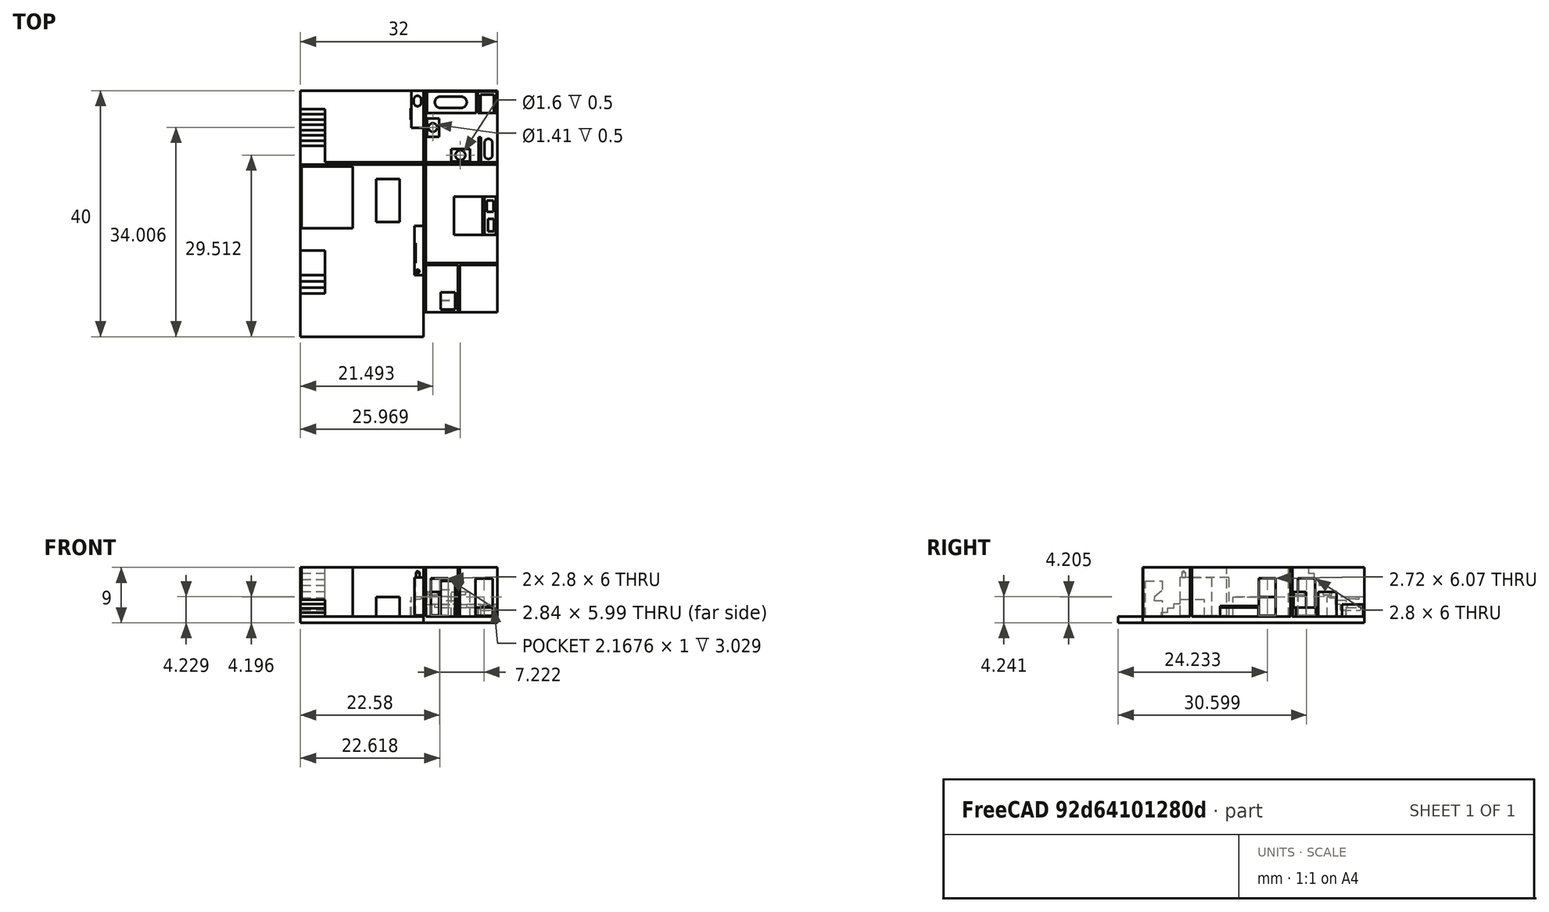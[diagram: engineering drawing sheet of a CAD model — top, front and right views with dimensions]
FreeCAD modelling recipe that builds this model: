
FCSTD DOCUMENT  (FreeCAD 0.19R)
Label: Addition1D_dualCloset
License: All rights reserved
LicenseURL: http://en.wikipedia.org/wiki/All_rights_reserved
objects: Sketcher::SketchObject×28, PartDesign::Pad×17, PartDesign::Pocket×10, PartDesign::Chamfer×1, PartDesign::Body×1, Mesh::Feature×1
note: 85 computed .brp shape members not serialized (recipe doc carries the construction recipe); baked Part::Feature solids carry a one-line shape summary decoded from their .brp

FEATURE [Sketcher::SketchObject] Sketch
  FullyConstrained = true
  MapMode = 5
  Support = -> [XY_Plane]
  sketch-geometry (8):
    g0: LineSegment StartX=0 StartY=-28 StartZ=0 EndX=-20 EndY=-28 EndZ=0
    g1: LineSegment StartX=-20 StartY=-28 StartZ=0 EndX=-20 EndY=0 EndZ=0
    g2: LineSegment StartX=-20 StartY=0 StartZ=0 EndX=-16 EndY=0 EndZ=0
    g3: LineSegment StartX=-16 StartY=0 StartZ=0 EndX=-16 EndY=12 EndZ=0
    g4: LineSegment StartX=-16 StartY=12 StartZ=0 EndX=12 EndY=12 EndZ=0
    g5: LineSegment StartX=12 StartY=12 StartZ=0 EndX=12 EndY=-24 EndZ=0
    g6: LineSegment StartX=12 StartY=-24 StartZ=0 EndX=0 EndY=-24 EndZ=0
    g7: LineSegment StartX=0 StartY=-24 StartZ=0 EndX=0 EndY=-28 EndZ=0
  constraints (24):
    c: Coincident(g0,g1)
    c: Horizontal(g0)
    c: Vertical(g1)
    c: DistanceX(g1) = -20
    c: DistanceY(g0) = -28
    c: Coincident(g1,g2)
    c: PointOnObject(g2,g-1)
    c: Horizontal(g2)
    c: Coincident(g2,g3)
    c: Vertical(g3)
    c: Coincident(g3,g4)
    c: Horizontal(g4)
    c: Coincident(g4,g5)
    c: Vertical(g5)
    c: Coincident(g5,g6)
    c: PointOnObject(g6,g-2)
    c: Coincident(g6,g7)
    c: Coincident(g7,g0)
    c: Vertical(g7)
    c: Horizontal(g6)
    c: Distance(g6) = 12
    c: Distance(g3) = 12
    c: DistanceY(g6) = -24
    c: DistanceX(g2) = -16
FEATURE [PartDesign::Pad] Pad  label="foundation"
  Direction = (1,1,1)
  Length = 1
  Length2 = 100
  Profile = -> Sketch
  Type = 0
FEATURE [Sketcher::SketchObject] Sketch004
  FullyConstrained = true
  MapMode = 5
  Placement = pos=(-16,0,0) rot=(0.57735,-0.57735,-0.57735;2.0944rad)
  Support = -> [Pad]
  sketch-geometry (20):
    g0: LineSegment StartX=-12 StartY=0 StartZ=0 EndX=-12 EndY=1 EndZ=0
    g1: LineSegment StartX=-12 StartY=1 StartZ=0 EndX=-9 EndY=1 EndZ=0
    g2: LineSegment StartX=-9 StartY=1 StartZ=0 EndX=-9 EndY=2 EndZ=0
    g3: LineSegment StartX=-9 StartY=2 StartZ=0 EndX=-8.14286 EndY=2 EndZ=0
    g4: LineSegment StartX=-8.14286 StartY=2 StartZ=0 EndX=-8.14286 EndY=3 EndZ=0
    g5: LineSegment StartX=-8.14286 StartY=3 StartZ=0 EndX=-7.28571 EndY=3 EndZ=0
    g6: LineSegment StartX=-7.28571 StartY=3 StartZ=0 EndX=-7.28571 EndY=4 EndZ=0
    g7: LineSegment StartX=-7.28571 StartY=4 StartZ=0 EndX=-6.42857 EndY=4 EndZ=0
    g8: LineSegment StartX=-6.42857 StartY=4 StartZ=0 EndX=-6.42857 EndY=5 EndZ=0
    g9: LineSegment StartX=-6.42857 StartY=5 StartZ=0 EndX=-5.57143 EndY=5 EndZ=0
    g10: LineSegment StartX=-5.57143 StartY=5 StartZ=0 EndX=-5.57143 EndY=6 EndZ=0
    g11: LineSegment StartX=-5.57143 StartY=6 StartZ=0 EndX=-4.71429 EndY=6 EndZ=0
    g12: LineSegment StartX=-4.71429 StartY=6 StartZ=0 EndX=-4.71429 EndY=7 EndZ=0
    g13: LineSegment StartX=-4.71429 StartY=7 StartZ=0 EndX=-3.85714 EndY=7 EndZ=0
    g14: LineSegment StartX=-3.85714 StartY=7 StartZ=0 EndX=-3.85714 EndY=8 EndZ=0
    g15: LineSegment StartX=-3.85714 StartY=8 StartZ=0 EndX=-3 EndY=8 EndZ=0
    g16: LineSegment StartX=-3 StartY=8 StartZ=0 EndX=-3 EndY=9 EndZ=0
    g17: LineSegment StartX=-3 StartY=9 StartZ=0 EndX=0 EndY=9 EndZ=0
    g18: LineSegment StartX=0 StartY=9 StartZ=0 EndX=0 EndY=0 EndZ=0
    g19: LineSegment StartX=0 StartY=0 StartZ=0 EndX=-12 EndY=0 EndZ=0
  constraints (59):
    c: PointOnObject(g0,g-1)
    c: Coincident(g0,g1)
    c: Coincident(g1,g2)
    c: Coincident(g2,g3)
    c: Coincident(g3,g4)
    c: Vertical(g4)
    c: Coincident(g4,g5)
    c: Horizontal(g5)
    c: Coincident(g5,g6)
    c: Coincident(g6,g7)
    c: Coincident(g7,g8)
    c: Coincident(g8,g9)
    c: Coincident(g9,g10)
    c: Coincident(g10,g11)
    c: Horizontal(g11)
    c: Coincident(g11,g12)
    c: Coincident(g12,g13)
    c: Coincident(g13,g14)
    c: Coincident(g14,g15)
    c: Coincident(g15,g16)
    c: Coincident(g16,g17)
    c: PointOnObject(g17,g-2)
    c: Coincident(g17,g18)
    c: Coincident(g18,g-1)
    c: Coincident(g18,g19)
    c: Coincident(g19,g0)
    c: DistanceY(g17) = 9
    c: Horizontal(g3)
    c: Horizontal(g7)
    c: Horizontal(g9)
    c: Horizontal(g13)
    c: Horizontal(g15)
    c: Vertical(g6)
    c: Vertical(g8)
    c: Vertical(g12)
    c: Vertical(g10)
    c: Vertical(g14)
    c: Vertical(g16)
    c: Vertical(g2)
    c: Equal(g2,g4)
    c: Equal(g4,g6)
    c: Equal(g6,g8)
    c: Equal(g8,g10)
    c: Equal(g10,g12)
    c: Equal(g12,g14)
    c: Equal(g14,g16)
    c: Distance(g17) = 3
    c: Equal(g3,g5)
    c: Equal(g5,g7)
    c: Equal(g7,g9)
    c: Equal(g9,g11)
    c: Equal(g11,g13)
    c: Equal(g13,g15)
    c: Horizontal(g1)
    c: Horizontal(g17)
    c: Distance(g1) = 3
    c: Vertical(g0)
    c: Distance(g0) = 1
    c: DistanceX(g0) = -12
FEATURE [Sketcher::SketchObject] Sketch007
  FullyConstrained = true
  MapMode = 5
  Placement = pos=(0,0,1) rot=(0,0,1;0rad)
  sketch-geometry (16):
    g0: LineSegment StartX=0.33 StartY=12 StartZ=0 EndX=0.33 EndY=-24 EndZ=0
    g1: LineSegment StartX=0.33 StartY=-24 StartZ=0 EndX=0 EndY=-24 EndZ=0
    g2: LineSegment StartX=0 StartY=-24 StartZ=0 EndX=0 EndY=12 EndZ=0
    g3: LineSegment StartX=0 StartY=12 StartZ=0 EndX=0.33 EndY=12 EndZ=0
    g4: LineSegment StartX=0.33 StartY=0.33 StartZ=0 EndX=12 EndY=0.33 EndZ=0
    g5: LineSegment StartX=12 StartY=0.33 StartZ=0 EndX=12 EndY=0 EndZ=0
    g6: LineSegment StartX=12 StartY=0 StartZ=0 EndX=0.33 EndY=0 EndZ=0
    g7: LineSegment StartX=0.33 StartY=0 StartZ=0 EndX=0.33 EndY=0.33 EndZ=0
    g8: LineSegment StartX=-16 StartY=0.33 StartZ=0 EndX=0 EndY=0.33 EndZ=0
    g9: LineSegment StartX=0 StartY=0.33 StartZ=0 EndX=0 EndY=0 EndZ=0
    g10: LineSegment StartX=0 StartY=0 StartZ=0 EndX=-16 EndY=0 EndZ=0
    g11: LineSegment StartX=-16 StartY=0 StartZ=0 EndX=-16 EndY=0.33 EndZ=0
    g12: LineSegment StartX=0.33 StartY=-16.33 StartZ=0 EndX=12 EndY=-16.33 EndZ=0
    g13: LineSegment StartX=12 StartY=-16.33 StartZ=0 EndX=12 EndY=-16 EndZ=0
    g14: LineSegment StartX=12 StartY=-16 StartZ=0 EndX=0.33 EndY=-16 EndZ=0
    g15: LineSegment StartX=0.33 StartY=-16 StartZ=0 EndX=0.33 EndY=-16.33 EndZ=0
  constraints (47):
    c: Coincident(g0,g1)
    c: Coincident(g1,g2)
    c: Horizontal(g1)
    c: Vertical(g0)
    c: Vertical(g2)
    c: DistanceY(g2) = 12
    c: PointOnObject(g-1,g2)
    c: Coincident(g3,g2)
    c: Coincident(g3,g0)
    c: Horizontal(g3)
    c: Distance(g3) = 0.33
    c: DistanceY(g0) = -24
    c: Coincident(g4,g5)
    c: Coincident(g5,g6)
    c: Coincident(g6,g7)
    c: Coincident(g7,g4)
    c: Horizontal(g4)
    c: Horizontal(g6)
    c: Vertical(g5)
    c: Vertical(g7)
    c: PointOnObject(g5,g-1)
    c: Coincident(g8,g9)
    c: Coincident(g9,g10)
    c: Coincident(g10,g11)
    c: Coincident(g11,g8)
    c: Horizontal(g8)
    c: Horizontal(g10)
    c: Vertical(g9)
    c: Vertical(g11)
    c: Coincident(g9,g-1)
    c: Coincident(g12,g13)
    c: Coincident(g13,g14)
    c: Coincident(g14,g15)
    c: Coincident(g15,g12)
    c: Horizontal(g12)
    c: Horizontal(g14)
    c: Vertical(g13)
    c: Vertical(g15)
    c: PointOnObject(g12,g0)
    c: Distance(g11) = 0.33
    c: Distance(g5) = 0.33
    c: DistanceX(g4) = 12
    c: DistanceX(g8) = -16
    c: PointOnObject(g4,g0)
    c: Distance(g13) = 0.33
    c: Distance(g0,g14) = 8
    c: DistanceX(g13) = 12
FEATURE [PartDesign::Pad] Pad004  label="wall"
  BaseFeature = -> Pad
  Direction = (1,1,1)
  Length = 8
  Length2 = 100
  Profile = -> Sketch007
  Type = 0
FEATURE [PartDesign::Pad] Pad005  label="stairs001"
  BaseFeature = -> Pad004
  Direction = (1,1,1)
  Length = 4
  Length2 = 100
  Profile = -> Sketch004
  Type = 0
FEATURE [Sketcher::SketchObject] Sketch008
  FullyConstrained = false
  MapMode = 5
  Placement = pos=(0,-16.33,0) rot=(1,0,0;1.5708rad)
  Support = -> [Pad005]
  sketch-geometry (8):
    g0: LineSegment StartX=1.18012 StartY=7.22945 StartZ=0 EndX=3.98012 EndY=7.22945 EndZ=0
    g1: LineSegment StartX=3.98012 StartY=7.22945 StartZ=0 EndX=3.98012 EndY=1.22945 EndZ=0
    g2: LineSegment StartX=3.98012 StartY=1.22945 StartZ=0 EndX=1.18012 EndY=1.22945 EndZ=0
    g3: LineSegment StartX=1.18012 StartY=1.22945 StartZ=0 EndX=1.18012 EndY=7.22945 EndZ=0
    g4: LineSegment StartX=8.40186 StartY=7.15703 StartZ=0 EndX=11.2019 EndY=7.15703 EndZ=0
    g5: LineSegment StartX=11.2019 StartY=7.15703 StartZ=0 EndX=11.2019 EndY=1.15703 EndZ=0
    g6: LineSegment StartX=11.2019 StartY=1.15703 StartZ=0 EndX=8.40186 EndY=1.15703 EndZ=0
    g7: LineSegment StartX=8.40186 StartY=1.15703 StartZ=0 EndX=8.40186 EndY=7.15703 EndZ=0
  constraints (20):
    c: Coincident(g0,g1)
    c: Coincident(g1,g2)
    c: Coincident(g2,g3)
    c: Coincident(g3,g0)
    c: Horizontal(g0)
    c: Horizontal(g2)
    c: Vertical(g1)
    c: Vertical(g3)
    c: Coincident(g4,g5)
    c: Coincident(g5,g6)
    c: Coincident(g6,g7)
    c: Coincident(g7,g4)
    c: Horizontal(g4)
    c: Horizontal(g6)
    c: Vertical(g5)
    c: Vertical(g7)
    c: Distance(g4) = 2.8
    c: Distance(g0) = 2.8
    c: Distance(g1) = 6
    c: Distance(g7) = 6
FEATURE [PartDesign::Pocket] Pocket
  BaseFeature = -> Pad005
  Length = 5
  Length2 = 100
  Profile = -> Sketch008
  Type = 0
FEATURE [Sketcher::SketchObject] Sketch009
  FullyConstrained = false
  MapMode = 5
  Placement = pos=(0,0,0) rot=(1,0,0;1.5708rad)
  Support = -> [Pocket]
  sketch-geometry (4):
    g0: LineSegment StartX=1.19795 StartY=7.19291 StartZ=0 EndX=4.03725 EndY=7.19291 EndZ=0
    g1: LineSegment StartX=4.03725 StartY=7.19291 StartZ=0 EndX=4.03725 EndY=1.19882 EndZ=0
    g2: LineSegment StartX=4.03725 StartY=1.19882 StartZ=0 EndX=1.19795 EndY=1.19882 EndZ=0
    g3: LineSegment StartX=1.19795 StartY=1.19882 StartZ=0 EndX=1.19795 EndY=7.19291 EndZ=0
  constraints (8):
    c: Coincident(g0,g1)
    c: Coincident(g1,g2)
    c: Coincident(g2,g3)
    c: Coincident(g3,g0)
    c: Horizontal(g0)
    c: Horizontal(g2)
    c: Vertical(g1)
    c: Vertical(g3)
FEATURE [PartDesign::Pocket] Pocket001
  BaseFeature = -> Pocket
  Length = 5
  Length2 = 100
  Profile = -> Sketch009
  Type = 0
FEATURE [Sketcher::SketchObject] Sketch010
  FullyConstrained = false
  MapMode = 5
  Placement = pos=(0.33,0,0) rot=(0.57735,0.57735,0.57735;2.0944rad)
  Support = -> [Pocket001]
  sketch-geometry (4):
    g0: LineSegment StartX=1.19868 StartY=7.24093 StartZ=0 EndX=3.99868 EndY=7.24093 EndZ=0
    g1: LineSegment StartX=3.99868 StartY=7.24093 StartZ=0 EndX=3.99868 EndY=1.24093 EndZ=0
    g2: LineSegment StartX=3.99868 StartY=1.24093 StartZ=0 EndX=1.19868 EndY=1.24093 EndZ=0
    g3: LineSegment StartX=1.19868 StartY=1.24093 StartZ=0 EndX=1.19868 EndY=7.24093 EndZ=0
  constraints (10):
    c: Coincident(g0,g1)
    c: Coincident(g1,g2)
    c: Coincident(g2,g3)
    c: Coincident(g3,g0)
    c: Horizontal(g0)
    c: Horizontal(g2)
    c: Vertical(g1)
    c: Vertical(g3)
    c: Distance(g0) = 2.8
    c: Distance(g1) = 6
FEATURE [PartDesign::Pocket] Pocket002
  BaseFeature = -> Pocket001
  Length = 5
  Length2 = 100
  Profile = -> Sketch010
  Type = 0
FEATURE [Sketcher::SketchObject] Sketch011
  FullyConstrained = false
  MapMode = 5
  Placement = pos=(0,0,1) rot=(0,0,1;0rad)
  Support = -> [Pocket002]
  sketch-geometry (8):
    g0: LineSegment StartX=0.512815 StartY=11.8677 StartZ=0 EndX=8.51282 EndY=11.8677 EndZ=0
    g1: LineSegment StartX=8.51282 StartY=11.8677 StartZ=0 EndX=8.51282 EndY=8.36765 EndZ=0
    g2: LineSegment StartX=8.51282 StartY=8.36765 StartZ=0 EndX=0.512815 EndY=8.36765 EndZ=0
    g3: LineSegment StartX=0.512815 StartY=8.36765 StartZ=0 EndX=0.512815 EndY=11.8677 EndZ=0
    g4: LineSegment StartX=8.80064 StartY=11.8358 StartZ=0 EndX=11.8627 EndY=11.8358 EndZ=0
    g5: LineSegment StartX=11.8627 StartY=11.8358 StartZ=0 EndX=11.8627 EndY=8.34693 EndZ=0
    g6: LineSegment StartX=11.8627 StartY=8.34693 StartZ=0 EndX=8.80064 EndY=8.34693 EndZ=0
    g7: LineSegment StartX=8.80064 StartY=8.34693 StartZ=0 EndX=8.80064 EndY=11.8358 EndZ=0
  constraints (18):
    c: Coincident(g0,g1)
    c: Coincident(g1,g2)
    c: Coincident(g2,g3)
    c: Coincident(g3,g0)
    c: Horizontal(g0)
    c: Horizontal(g2)
    c: Vertical(g1)
    c: Vertical(g3)
    c: Coincident(g4,g5)
    c: Coincident(g5,g6)
    c: Coincident(g6,g7)
    c: Coincident(g7,g4)
    c: Horizontal(g4)
    c: Horizontal(g6)
    c: Vertical(g5)
    c: Vertical(g7)
    c: Distance(g0) = 8
    c: Distance(g1) = 3.5
FEATURE [PartDesign::Pad] Pad006
  BaseFeature = -> Pocket002
  Direction = (1,1,1)
  Length = 2
  Length2 = 100
  Profile = -> Sketch011
  Type = 0
FEATURE [Sketcher::SketchObject] Sketch012
  FullyConstrained = false
  MapMode = 5
  Placement = pos=(0,0,1) rot=(0,0,1;0rad)
  Support = -> [Pad006]
  sketch-geometry (8):
    g0: LineSegment StartX=4.5 StartY=2.51571 StartZ=0 EndX=7.5 EndY=2.51571 EndZ=0
    g1: LineSegment StartX=7.5 StartY=2.51571 StartZ=0 EndX=7.5 EndY=0.515713 EndZ=0
    g2: LineSegment StartX=7.5 StartY=0.515713 StartZ=0 EndX=4.5 EndY=0.515713 EndZ=0
    g3: LineSegment StartX=4.5 StartY=0.515713 StartZ=0 EndX=4.5 EndY=2.51571 EndZ=0
    g4: LineSegment StartX=0.518943 StartY=7.5 StartZ=0 EndX=2.51894 EndY=7.5 EndZ=0
    g5: LineSegment StartX=2.51894 StartY=7.5 StartZ=0 EndX=2.51894 EndY=4.5 EndZ=0
    g6: LineSegment StartX=2.51894 StartY=4.5 StartZ=0 EndX=0.518943 EndY=4.5 EndZ=0
    g7: LineSegment StartX=0.518943 StartY=4.5 StartZ=0 EndX=0.518943 EndY=7.5 EndZ=0
  constraints (22):
    c: Coincident(g0,g1)
    c: Coincident(g1,g2)
    c: Coincident(g2,g3)
    c: Coincident(g3,g0)
    c: Horizontal(g0)
    c: Horizontal(g2)
    c: Vertical(g1)
    c: Vertical(g3)
    c: Distance(g3) = 2
    c: Distance(g0) = 3
    c: Coincident(g4,g5)
    c: Coincident(g5,g6)
    c: Coincident(g6,g7)
    c: Coincident(g7,g4)
    c: Horizontal(g4)
    c: Horizontal(g6)
    c: Vertical(g5)
    c: Vertical(g7)
    c: Distance(g4) = 2
    c: Distance(g5) = 3
    c: DistanceY(g6) = 4.5
    c: DistanceX(g2) = 4.5
FEATURE [PartDesign::Pad] Pad007
  BaseFeature = -> Pad006
  Direction = (1,1,1)
  Length = 4
  Length2 = 100
  Profile = -> Sketch012
  Type = 0
FEATURE [Sketcher::SketchObject] Sketch013
  FullyConstrained = false
  MapMode = 5
  Placement = pos=(0,0,1) rot=(0,0,1;0rad)
  Support = -> [Pad007]
  sketch-geometry (8):
    g0: LineSegment StartX=8.91387 StartY=4.41728 StartZ=0 EndX=9.28193 EndY=4.41728 EndZ=0
    g1: LineSegment StartX=9.28193 StartY=4.41728 StartZ=0 EndX=9.28193 EndY=0.342351 EndZ=0
    g2: LineSegment StartX=9.28193 StartY=0.342351 StartZ=0 EndX=8.91387 EndY=0.342351 EndZ=0
    g3: LineSegment StartX=8.91387 StartY=0.342351 StartZ=0 EndX=8.91387 EndY=4.41728 EndZ=0
    g4: ArcOfCircle CenterX=10.5176 CenterY=3.49717 CenterZ=0 NormalX=0 NormalY=0 NormalZ=1 AngleXU=0 Radius=0.657223 StartAngle=0 EndAngle=3.14159
    g5: ArcOfCircle CenterX=10.5176 CenterY=1.55168 CenterZ=0 NormalX=0 NormalY=0 NormalZ=1 AngleXU=0 Radius=0.657223 StartAngle=3.14159 EndAngle=6.28319
    g6: LineSegment StartX=9.86033 StartY=3.49717 StartZ=0 EndX=9.86033 EndY=1.55168 EndZ=0
    g7: LineSegment StartX=11.1748 StartY=3.49717 StartZ=0 EndX=11.1748 EndY=1.55168 EndZ=0
  constraints (14):
    c: Coincident(g0,g1)
    c: Coincident(g1,g2)
    c: Coincident(g2,g3)
    c: Coincident(g3,g0)
    c: Horizontal(g0)
    c: Horizontal(g2)
    c: Vertical(g1)
    c: Vertical(g3)
    c: Tangent(g4,g7) = 1.5708
    c: Tangent(g4,g6) = -1.5708
    c: Tangent(g6,g5) = -1.5708
    c: Tangent(g7,g5) = 1.5708
    c: Vertical(g6)
    c: Equal(g4,g5)
FEATURE [PartDesign::Pad] Pad008
  BaseFeature = -> Pad007
  Direction = (1,1,1)
  Length = 1.5
  Length2 = 100
  Profile = -> Sketch013
  Type = 0
FEATURE [Sketcher::SketchObject] Sketch014
  FullyConstrained = false
  MapMode = 5
  Placement = pos=(0,0,3) rot=(0,0,1;0rad)
  Support = -> [Pad008]
  sketch-geometry (4):
    g0: ArcOfCircle CenterX=2.72003 CenterY=10.1095 CenterZ=0 NormalX=0 NormalY=0 NormalZ=1 AngleXU=0 Radius=0.911861 StartAngle=1.5708 EndAngle=4.71239
    g1: ArcOfCircle CenterX=6.09294 CenterY=10.1095 CenterZ=0 NormalX=0 NormalY=0 NormalZ=1 AngleXU=0 Radius=0.911861 StartAngle=4.71239 EndAngle=7.85398
    g2: LineSegment StartX=2.72003 StartY=9.1976 StartZ=0 EndX=6.09294 EndY=9.1976 EndZ=0
    g3: LineSegment StartX=2.72003 StartY=11.0213 StartZ=0 EndX=6.09294 EndY=11.0213 EndZ=0
  constraints (6):
    c: Tangent(g0,g3) = 1.5708
    c: Tangent(g0,g2) = -1.5708
    c: Tangent(g2,g1) = -1.5708
    c: Tangent(g3,g1) = 1.5708
    c: Horizontal(g2)
    c: Equal(g0,g1)
FEATURE [PartDesign::Pocket] Pocket003
  BaseFeature = -> Pad008
  Length = 0.5
  Length2 = 100
  Profile = -> Sketch014
  Type = 0
FEATURE [Sketcher::SketchObject] Sketch015
  FullyConstrained = false
  MapMode = 5
  Placement = pos=(0,0,5) rot=(0,0,1;0rad)
  Support = -> [Pocket003]
  sketch-geometry (2):
    g0: Circle CenterX=1.49285 CenterY=6.00605 CenterZ=0 NormalX=0 NormalY=0 NormalZ=1 AngleXU=0 Radius=0.704239
    g1: Circle CenterX=5.96899 CenterY=1.51228 CenterZ=0 NormalX=0 NormalY=0 NormalZ=1 AngleXU=0 Radius=0.797608
FEATURE [PartDesign::Pocket] Pocket004
  BaseFeature = -> Pocket003
  Length = 0.5
  Length2 = 100
  Profile = -> Sketch015
  Type = 0
FEATURE [Sketcher::SketchObject] Sketch016
  FullyConstrained = false
  MapMode = 5
  Placement = pos=(0,0,3) rot=(0,0,1;0rad)
  Support = -> [Pocket004]
  sketch-geometry (4):
    g0: LineSegment StartX=9.25841 StartY=11.3759 StartZ=0 EndX=11.426 EndY=11.3759 EndZ=0
    g1: LineSegment StartX=11.426 StartY=11.3759 StartZ=0 EndX=11.426 EndY=7.14651 EndZ=0
    g2: LineSegment StartX=11.426 StartY=7.14651 StartZ=0 EndX=9.25841 EndY=7.14651 EndZ=0
    g3: LineSegment StartX=9.25841 StartY=7.14651 StartZ=0 EndX=9.25841 EndY=11.3759 EndZ=0
  constraints (8):
    c: Coincident(g0,g1)
    c: Coincident(g1,g2)
    c: Coincident(g2,g3)
    c: Coincident(g3,g0)
    c: Horizontal(g0)
    c: Horizontal(g2)
    c: Vertical(g1)
    c: Vertical(g3)
FEATURE [PartDesign::Pocket] Pocket005
  BaseFeature = -> Pocket004
  Length = 1
  Length2 = 100
  Profile = -> Sketch016
  Type = 0
FEATURE [Sketcher::SketchObject] Sketch017
  FullyConstrained = false
  MapMode = 5
  Placement = pos=(0.33,0,0) rot=(0.57735,0.57735,0.57735;2.0944rad)
  Support = -> [Pocket005]
  sketch-geometry (4):
    g0: LineSegment StartX=-5.12452 StartY=7.24184 StartZ=0 EndX=-2.40892 EndY=7.24184 EndZ=0
    g1: LineSegment StartX=-2.40892 StartY=7.24184 StartZ=0 EndX=-2.40892 EndY=1.16746 EndZ=0
    g2: LineSegment StartX=-2.40892 StartY=1.16746 StartZ=0 EndX=-5.12452 EndY=1.16746 EndZ=0
    g3: LineSegment StartX=-5.12452 StartY=1.16746 StartZ=0 EndX=-5.12452 EndY=7.24184 EndZ=0
  constraints (8):
    c: Coincident(g0,g1)
    c: Coincident(g1,g2)
    c: Coincident(g2,g3)
    c: Coincident(g3,g0)
    c: Horizontal(g0)
    c: Horizontal(g2)
    c: Vertical(g1)
    c: Vertical(g3)
FEATURE [PartDesign::Pocket] Pocket006
  BaseFeature = -> Pocket005
  Length = 5
  Length2 = 100
  Profile = -> Sketch017
  Type = 0
FEATURE [Sketcher::SketchObject] Sketch018
  FullyConstrained = false
  MapMode = 5
  Placement = pos=(0,0,0) rot=(0.57735,-0.57735,-0.57735;2.0944rad)
  Support = -> [Pocket006]
  sketch-geometry (4):
    g0: LineSegment StartX=10 StartY=7.38099 StartZ=0 EndX=18 EndY=7.38099 EndZ=0
    g1: LineSegment StartX=18 StartY=7.38099 StartZ=0 EndX=18 EndY=1.18099 EndZ=0
    g2: LineSegment StartX=18 StartY=1.18099 StartZ=0 EndX=10 EndY=1.18099 EndZ=0
    g3: LineSegment StartX=10 StartY=1.18099 StartZ=0 EndX=10 EndY=7.38099 EndZ=0
  constraints (11):
    c: Coincident(g0,g1)
    c: Coincident(g1,g2)
    c: Coincident(g2,g3)
    c: Coincident(g3,g0)
    c: Horizontal(g0)
    c: Horizontal(g2)
    c: Vertical(g1)
    c: Vertical(g3)
    c: Distance(g0) = 8
    c: DistanceX(g0) = 10
    c: Distance(g1) = 6.2
FEATURE [PartDesign::Pad] Pad009
  BaseFeature = -> Pocket006
  Direction = (1,1,1)
  Length = 1.5
  Length2 = 100
  Profile = -> Sketch018
  Type = 0
FEATURE [Sketcher::SketchObject] Sketch019
  FullyConstrained = false
  MapMode = 5
  Placement = pos=(0,0,1) rot=(0,0,1;0rad)
  Support = -> [Pad009]
  sketch-geometry (4):
    g0: LineSegment StartX=-19.8609 StartY=-0.34413 StartZ=0 EndX=-11.5 EndY=-0.34413 EndZ=0
    g1: LineSegment StartX=-11.5 StartY=-0.34413 StartZ=0 EndX=-11.5 EndY=-10.3441 EndZ=0
    g2: LineSegment StartX=-11.5 StartY=-10.3441 StartZ=0 EndX=-19.8609 EndY=-10.3441 EndZ=0
    g3: LineSegment StartX=-19.8609 StartY=-10.3441 StartZ=0 EndX=-19.8609 EndY=-0.34413 EndZ=0
  constraints (10):
    c: Coincident(g0,g1)
    c: Coincident(g1,g2)
    c: Coincident(g2,g3)
    c: Coincident(g3,g0)
    c: Horizontal(g0)
    c: Horizontal(g2)
    c: Vertical(g1)
    c: Vertical(g3)
    c: DistanceX(g0) = -11.5
    c: Distance(g1) = 10
FEATURE [PartDesign::Pad] Pad010
  BaseFeature = -> Pad009
  Direction = (1,1,1)
  Length = 8
  Length2 = 100
  Profile = -> Sketch019
  Type = 0
FEATURE [Sketcher::SketchObject] Sketch022
  FullyConstrained = false
  MapMode = 5
  Placement = pos=(-20,0,0) rot=(0.57735,-0.57735,-0.57735;2.0944rad)
  Support = -> [Pad010]
  sketch-geometry (10):
    g0: LineSegment StartX=21 StartY=0.958354 StartZ=0 EndX=14 EndY=0.958354 EndZ=0
    g1: LineSegment StartX=14 StartY=0.958354 StartZ=0 EndX=14 EndY=3.75835 EndZ=0
    g2: LineSegment StartX=14 StartY=3.75835 StartZ=0 EndX=18 EndY=3.75835 EndZ=0
    g3: LineSegment StartX=18 StartY=3.75835 StartZ=0 EndX=18 EndY=3.05835 EndZ=0
    g4: LineSegment StartX=18 StartY=3.05835 StartZ=0 EndX=19 EndY=3.05835 EndZ=0
    g5: LineSegment StartX=19 StartY=3.05835 StartZ=0 EndX=19 EndY=2.35835 EndZ=0
    g6: LineSegment StartX=19 StartY=2.35835 StartZ=0 EndX=20 EndY=2.35835 EndZ=0
    g7: LineSegment StartX=20 StartY=2.35835 StartZ=0 EndX=20 EndY=1.65835 EndZ=0
    g8: LineSegment StartX=20 StartY=1.65835 StartZ=0 EndX=21 EndY=1.65835 EndZ=0
    g9: LineSegment StartX=21 StartY=1.65835 StartZ=0 EndX=21 EndY=0.958354 EndZ=0
  constraints (29):
    c: Coincident(g0,g1)
    c: Horizontal(g0)
    c: Vertical(g1)
    c: Distance(g1) = 2.8
    c: DistanceX(g1) = 14
    c: Coincident(g1,g2)
    c: Horizontal(g2)
    c: Coincident(g2,g3)
    c: Coincident(g3,g4)
    c: Coincident(g4,g5)
    c: Coincident(g5,g6)
    c: Coincident(g6,g7)
    c: Coincident(g7,g8)
    c: Coincident(g8,g9)
    c: Coincident(g0,g9)
    c: Vertical(g9)
    c: Vertical(g7)
    c: Vertical(g5)
    c: Vertical(g3)
    c: Distance(g0) = 7
    c: Equal(g8,g6)
    c: Equal(g6,g4)
    c: Horizontal(g8)
    c: Horizontal(g6)
    c: Horizontal(g4)
    c: Equal(g3,g5)
    c: Equal(g5,g7)
    c: Equal(g7,g9)
    c: Distance(g2) = 4
FEATURE [PartDesign::Pad] Pad011
  BaseFeature = -> Pad010
  Direction = (1,1,1)
  Length = 4
  Length2 = 100
  Profile = -> Sketch022
  Reversed = true
  Type = 0
FEATURE [Sketcher::SketchObject] Sketch023
  FullyConstrained = false
  MapMode = 5
  Placement = pos=(0,0,1) rot=(0,0,1;0rad)
  Support = -> [Pad011]
  sketch-geometry (4):
    g0: LineSegment StartX=5.57555 StartY=-16.2289 StartZ=0 EndX=5.90555 EndY=-16.2289 EndZ=0
    g1: LineSegment StartX=5.90555 StartY=-16.2289 StartZ=0 EndX=5.90555 EndY=-23.9704 EndZ=0
    g2: LineSegment StartX=5.90555 StartY=-23.9704 StartZ=0 EndX=5.57555 EndY=-23.9704 EndZ=0
    g3: LineSegment StartX=5.57555 StartY=-23.9704 StartZ=0 EndX=5.57555 EndY=-16.2289 EndZ=0
  constraints (9):
    c: Coincident(g0,g1)
    c: Coincident(g1,g2)
    c: Coincident(g2,g3)
    c: Coincident(g3,g0)
    c: Horizontal(g0)
    c: Horizontal(g2)
    c: Vertical(g1)
    c: Vertical(g3)
    c: Distance(g2) = 0.33
FEATURE [PartDesign::Pad] Pad012  label="BRdirvider"
  BaseFeature = -> Pad011
  Direction = (1,1,1)
  Length = 8
  Length2 = 100
  Profile = -> Sketch023
  Type = 0
FEATURE [Sketcher::SketchObject] Sketch024  label="kitchenette"
  FullyConstrained = false
  MapMode = 5
  Placement = pos=(0,0,1) rot=(0,0,1;0rad)
  Support = -> [Pad012]
  sketch-geometry (4):
    g0: LineSegment StartX=-1.99946 StartY=11.9634 StartZ=0 EndX=0.000542712 EndY=11.9634 EndZ=0
    g1: LineSegment StartX=0.000542712 StartY=11.9634 StartZ=0 EndX=0.000542712 EndY=5.9634 EndZ=0
    g2: LineSegment StartX=0.000542712 StartY=5.9634 StartZ=0 EndX=-1.99946 EndY=5.9634 EndZ=0
    g3: LineSegment StartX=-1.99946 StartY=5.9634 StartZ=0 EndX=-1.99946 EndY=11.9634 EndZ=0
  constraints (10):
    c: Coincident(g0,g1)
    c: Vertical(g1)
    c: Coincident(g1,g2)
    c: Coincident(g2,g3)
    c: Coincident(g3,g0)
    c: Vertical(g3)
    c: Horizontal(g2)
    c: Distance(g2) = 2
    c: Horizontal(g0)
    c: Distance(g1) = 6
FEATURE [PartDesign::Pad] Pad013
  BaseFeature = -> Pad012
  Direction = (1,1,1)
  Length = 3.2
  Length2 = 100
  Profile = -> Sketch024
  Type = 0
FEATURE [Sketcher::SketchObject] Sketch025
  FullyConstrained = false
  MapMode = 5
  Placement = pos=(0,0,4.2) rot=(0,0,1;0rad)
  Support = -> [Pad013]
  sketch-geometry (4):
    g0: ArcOfCircle CenterX=-0.997239 CenterY=10.5422 CenterZ=0 NormalX=0 NormalY=0 NormalZ=1 AngleXU=0 Radius=0.606949 StartAngle=0 EndAngle=3.14159
    g1: ArcOfCircle CenterX=-0.997239 CenterY=10.069 CenterZ=0 NormalX=0 NormalY=0 NormalZ=1 AngleXU=0 Radius=0.606949 StartAngle=3.14159 EndAngle=6.28319
    g2: LineSegment StartX=-1.60419 StartY=10.5422 StartZ=0 EndX=-1.60419 EndY=10.069 EndZ=0
    g3: LineSegment StartX=-0.39029 StartY=10.5422 StartZ=0 EndX=-0.39029 EndY=10.069 EndZ=0
  constraints (6):
    c: Tangent(g0,g3) = 1.5708
    c: Tangent(g0,g2) = -1.5708
    c: Tangent(g2,g1) = -1.5708
    c: Tangent(g3,g1) = 1.5708
    c: Vertical(g2)
    c: Equal(g0,g1)
FEATURE [PartDesign::Pocket] Pocket007
  BaseFeature = -> Pad013
  Length = 0.35
  Length2 = 100
  Profile = -> Sketch025
  Type = 0
FEATURE [Sketcher::SketchObject] Sketch026
  FullyConstrained = false
  MapMode = 5
  Placement = pos=(-1.99946,0,0) rot=(0.57735,-0.57735,-0.57735;2.0944rad)
  Support = -> [Pocket007]
  sketch-geometry (4):
    g0: LineSegment StartX=-9.10306 StartY=3.58683 StartZ=0 EndX=-7.30306 EndY=3.58683 EndZ=0
    g1: LineSegment StartX=-7.30306 StartY=3.58683 StartZ=0 EndX=-7.30306 EndY=1.08683 EndZ=0
    g2: LineSegment StartX=-7.30306 StartY=1.08683 StartZ=0 EndX=-9.10306 EndY=1.08683 EndZ=0
    g3: LineSegment StartX=-9.10306 StartY=1.08683 StartZ=0 EndX=-9.10306 EndY=3.58683 EndZ=0
  constraints (10):
    c: Coincident(g0,g1)
    c: Coincident(g1,g2)
    c: Coincident(g2,g3)
    c: Coincident(g3,g0)
    c: Horizontal(g0)
    c: Horizontal(g2)
    c: Vertical(g1)
    c: Vertical(g3)
    c: Distance(g0) = 1.8
    c: Distance(g3) = 2.5
FEATURE [PartDesign::Pad] Pad014  label="icemaker"
  BaseFeature = -> Pocket007
  Direction = (1,1,1)
  Length = 0.1
  Length2 = 100
  Profile = -> Sketch026
  Type = 0
FEATURE [Sketcher::SketchObject] Sketch027
  FullyConstrained = false
  MapMode = 5
  Placement = pos=(-1.5,0,0) rot=(0.57735,-0.57735,-0.57735;2.0944rad)
  Support = -> [Pad014]
  sketch-geometry (4):
    g0: LineSegment StartX=12.755 StartY=7.45922 StartZ=0 EndX=16.0051 EndY=7.45922 EndZ=0
    g1: LineSegment StartX=16.0051 StartY=7.45922 StartZ=0 EndX=16.0051 EndY=1.21717 EndZ=0
    g2: LineSegment StartX=16.0051 StartY=1.21717 StartZ=0 EndX=12.755 EndY=1.21717 EndZ=0
    g3: LineSegment StartX=12.755 StartY=1.21717 StartZ=0 EndX=12.755 EndY=7.45922 EndZ=0
  constraints (8):
    c: Coincident(g0,g1)
    c: Coincident(g1,g2)
    c: Coincident(g2,g3)
    c: Coincident(g3,g0)
    c: Horizontal(g0)
    c: Horizontal(g2)
    c: Vertical(g1)
    c: Vertical(g3)
FEATURE [PartDesign::Pocket] Pocket008
  BaseFeature = -> Pad014
  Length = 0.2
  Length2 = 100
  Profile = -> Sketch027
  Type = 0
FEATURE [Sketcher::SketchObject] Sketch028
  FullyConstrained = false
  MapMode = 5
  Placement = pos=(0,0,7.38099) rot=(0,0,1;0rad)
  Support = -> [Pocket008]
  sketch-geometry (1):
    g0: Circle CenterX=-0.970954 CenterY=-17.3767 CenterZ=0 NormalX=0 NormalY=0 NormalZ=1 AngleXU=0 Radius=0.280145
FEATURE [PartDesign::Pad] Pad015
  BaseFeature = -> Pocket008
  Direction = (1,1,1)
  Length = 1
  Length2 = 100
  Profile = -> Sketch028
  Type = 0
FEATURE [PartDesign::Chamfer] Chamfer
  Angle = 45
  Base = -> Pad015 [Edge377]
  BaseFeature = -> Pad015
  ChamferType = 0
  FlipDirection = false
  Size = 0.2
  Size2 = 1
  SupportTransform = false
FEATURE [Sketcher::SketchObject] Sketch033
  FullyConstrained = false
  MapMode = 5
  Placement = pos=(0,0,1) rot=(0,0,1;0rad)
  Support = -> [Chamfer]
  sketch-geometry (4):
    g0: LineSegment StartX=2.74629 StartY=-20.7806 StartZ=0 EndX=5.14629 EndY=-20.7806 EndZ=0
    g1: LineSegment StartX=5.14629 StartY=-20.7806 StartZ=0 EndX=5.14629 EndY=-23.5806 EndZ=0
    g2: LineSegment StartX=5.14629 StartY=-23.5806 StartZ=0 EndX=2.74629 EndY=-23.5806 EndZ=0
    g3: LineSegment StartX=2.74629 StartY=-23.5806 StartZ=0 EndX=2.74629 EndY=-20.7806 EndZ=0
  constraints (10):
    c: Coincident(g0,g1)
    c: Coincident(g1,g2)
    c: Coincident(g2,g3)
    c: Coincident(g3,g0)
    c: Horizontal(g0)
    c: Horizontal(g2)
    c: Vertical(g1)
    c: Vertical(g3)
    c: Distance(g0) = 2.4
    c: Distance(g3) = 2.8
FEATURE [PartDesign::Pad] Pad016
  BaseFeature = -> Chamfer
  Direction = (1,1,1)
  Length = 5.8
  Length2 = 100
  Profile = -> Sketch033
  Type = 0
FEATURE [Sketcher::SketchObject] Sketch034
  FullyConstrained = false
  MapMode = 5
  Placement = pos=(2.74629,0,0) rot=(0.57735,-0.57735,-0.57735;2.0944rad)
  Support = -> [Pad016]
  sketch-geometry (4):
    g0: LineSegment StartX=20.6066 StartY=3.56678 StartZ=0 EndX=22.097 EndY=3.56678 EndZ=0
    g1: LineSegment StartX=22.097 StartY=3.56678 StartZ=0 EndX=22.0697 EndY=4.30513 EndZ=0
    g2: LineSegment StartX=22.0697 StartY=4.30513 StartZ=0 EndX=20.6066 EndY=5.53571 EndZ=0
    g3: LineSegment StartX=20.6066 StartY=5.53571 StartZ=0 EndX=20.6066 EndY=3.56678 EndZ=0
  constraints (6):
    c: Horizontal(g0)
    c: Coincident(g0,g1)
    c: Coincident(g1,g2)
    c: Coincident(g2,g3)
    c: Coincident(g3,g0)
    c: Vertical(g3)
FEATURE [PartDesign::Pocket] Pocket009
  BaseFeature = -> Pad016
  Length = 2.5
  Length2 = 100
  Profile = -> Sketch034
  Type = 0
FEATURE [Sketcher::SketchObject] Sketch035
  FullyConstrained = true
  MapMode = 5
  Placement = pos=(0,0,0) rot=(1,0,0;3.14159rad)
  Support = -> [Pocket009]
FEATURE [Sketcher::SketchObject] Sketch036
  FullyConstrained = false
  MapMode = 5
  Placement = pos=(0,0,1) rot=(0,0,1;0rad)
  Support = -> [Pocket009]
  sketch-geometry (4):
    g0: LineSegment StartX=-7.7165 StartY=-2.34711 StartZ=0 EndX=-3.9165 EndY=-2.34711 EndZ=0
    g1: LineSegment StartX=-3.9165 StartY=-2.34711 StartZ=0 EndX=-3.9165 EndY=-9.34711 EndZ=0
    g2: LineSegment StartX=-3.9165 StartY=-9.34711 StartZ=0 EndX=-7.7165 EndY=-9.34711 EndZ=0
    g3: LineSegment StartX=-7.7165 StartY=-9.34711 StartZ=0 EndX=-7.7165 EndY=-2.34711 EndZ=0
  constraints (10):
    c: Coincident(g0,g1)
    c: Coincident(g1,g2)
    c: Coincident(g2,g3)
    c: Coincident(g3,g0)
    c: Horizontal(g0)
    c: Horizontal(g2)
    c: Vertical(g1)
    c: Vertical(g3)
    c: Distance(g0) = 3.8
    c: Distance(g3) = 7
FEATURE [PartDesign::Pad] Pad017
  BaseFeature = -> Pocket009
  Direction = (1,1,1)
  Length = 3.2
  Length2 = 100
  Profile = -> Sketch036
  Type = 0
FEATURE [Sketcher::SketchObject] Sketch037
  FullyConstrained = false
  MapMode = 5
  Placement = pos=(0,0,1) rot=(0,0,1;0rad)
  Support = -> [Pad017]
  sketch-geometry (4):
    g0: LineSegment StartX=4.92681 StartY=-5.23214 StartZ=0 EndX=11.7268 EndY=-5.23214 EndZ=0
    g1: LineSegment StartX=11.7268 StartY=-5.23214 StartZ=0 EndX=11.7268 EndY=-11.4321 EndZ=0
    g2: LineSegment StartX=11.7268 StartY=-11.4321 StartZ=0 EndX=4.92681 EndY=-11.4321 EndZ=0
    g3: LineSegment StartX=4.92681 StartY=-11.4321 StartZ=0 EndX=4.92681 EndY=-5.23214 EndZ=0
  constraints (10):
    c: Coincident(g0,g1)
    c: Coincident(g1,g2)
    c: Coincident(g2,g3)
    c: Coincident(g3,g0)
    c: Horizontal(g0)
    c: Horizontal(g2)
    c: Vertical(g1)
    c: Vertical(g3)
    c: Distance(g1) = 6.2
    c: Distance(g0) = 6.8
FEATURE [PartDesign::Pad] Pad018
  BaseFeature = -> Pad017
  Direction = (1,1,1)
  Length = 1.5
  Length2 = 100
  Profile = -> Sketch037
  Type = 0
FEATURE [Sketcher::SketchObject] Sketch038
  FullyConstrained = false
  MapMode = 5
  Placement = pos=(0,0,2.5) rot=(0,0,1;0rad)
  Support = -> [Pad018]
  sketch-geometry (12):
    g0: LineSegment StartX=9.53341 StartY=-5.24295 StartZ=0 EndX=9.88639 EndY=-5.24295 EndZ=0
    g1: LineSegment StartX=9.88639 StartY=-5.24295 StartZ=0 EndX=9.88639 EndY=-11.4476 EndZ=0
    g2: LineSegment StartX=9.88639 StartY=-11.4476 StartZ=0 EndX=9.53341 EndY=-11.4476 EndZ=0
    g3: LineSegment StartX=9.53341 StartY=-11.4476 StartZ=0 EndX=9.53341 EndY=-5.24295 EndZ=0
    g4: LineSegment StartX=10.2899 StartY=-5.85344 StartZ=0 EndX=11.3415 EndY=-5.85344 EndZ=0
    g5: LineSegment StartX=11.3415 StartY=-5.85344 StartZ=0 EndX=11.3415 EndY=-7.69373 EndZ=0
    g6: LineSegment StartX=11.3415 StartY=-7.69373 StartZ=0 EndX=10.2899 EndY=-7.69373 EndZ=0
    g7: LineSegment StartX=10.2899 StartY=-7.69373 StartZ=0 EndX=10.2899 EndY=-5.85344 EndZ=0
    g8: LineSegment StartX=10.4477 StartY=-8.87677 StartZ=0 EndX=11.3941 EndY=-8.87677 EndZ=0
    g9: LineSegment StartX=11.3941 StartY=-8.87677 StartZ=0 EndX=11.3941 EndY=-10.8485 EndZ=0
    g10: LineSegment StartX=11.3941 StartY=-10.8485 StartZ=0 EndX=10.4477 EndY=-10.8485 EndZ=0
    g11: LineSegment StartX=10.4477 StartY=-10.8485 StartZ=0 EndX=10.4477 EndY=-8.87677 EndZ=0
  constraints (24):
    c: Coincident(g0,g1)
    c: Coincident(g1,g2)
    c: Coincident(g2,g3)
    c: Coincident(g3,g0)
    c: Horizontal(g0)
    c: Horizontal(g2)
    c: Vertical(g1)
    c: Vertical(g3)
    c: Coincident(g4,g5)
    c: Coincident(g5,g6)
    c: Coincident(g6,g7)
    c: Coincident(g7,g4)
    c: Horizontal(g4)
    c: Horizontal(g6)
    c: Vertical(g5)
    c: Vertical(g7)
    c: Coincident(g8,g9)
    c: Coincident(g9,g10)
    c: Coincident(g10,g11)
    c: Coincident(g11,g8)
    c: Horizontal(g8)
    c: Horizontal(g10)
    c: Vertical(g9)
    c: Vertical(g11)
FEATURE [PartDesign::Pad] Pad019
  BaseFeature = -> Pad018
  Direction = (1,1,1)
  Length = 0.2
  Length2 = 100
  Profile = -> Sketch038
  Type = 0
FEATURE [PartDesign::Body] Body
  Group = -> [Sketch,Pad,Sketch004,Sketch007,Pad004,Pad005,Sketch008,Pocket,Sketch009,Pocket001,Sketch010,Pocket002,Sketch011,Pad006,Sketch012,Pad007,Sketch013,Pad008,Sketch014,Pocket003,Sketch015,Pocket004,Sketch016,Pocket005,Sketch017,Pocket006,Sketch018,Pad009,Sketch019,Pad010,Sketch022,Pad011,Sketch023,Pad012,Sketch024,Pad013,Sketch025,Pocket007,Sketch026,Pad014,Sketch027,Pocket008,Sketch028,Pad015,Chamfer,+11 more]
  Origin = -> Origin
  Tip = -> Pad019
FEATURE [Mesh::Feature] Mesh  label="Pad019 (Meshed)"
